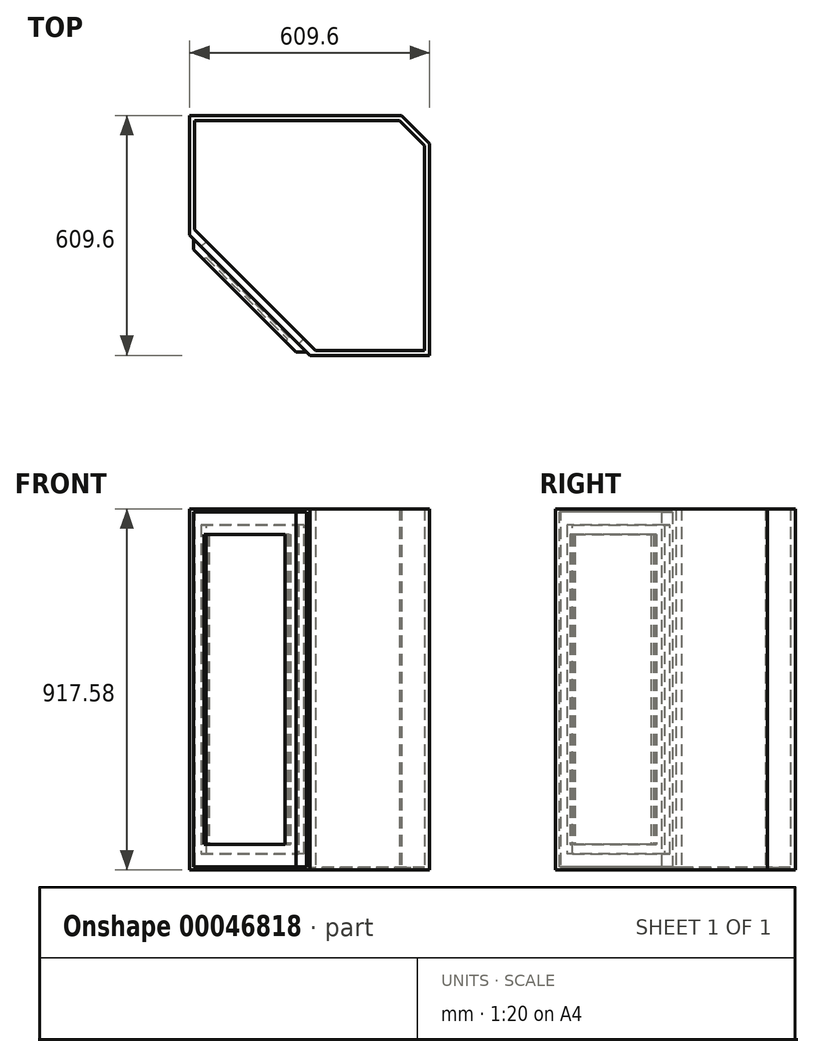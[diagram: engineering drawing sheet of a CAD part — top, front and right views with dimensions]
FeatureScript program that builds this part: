
annotation { "Feature Type Name" : "Feature", "Feature Type Description" : "" }
export const myFeature = defineFeature(function(context is Context, id is Id, definition is map)
    precondition{}
    {
        {
            var Q0;
            Q0=qCreatedBy(makeId("Top.planeOp"),FACE);
            var sketch = newSketch(context, id + "F0", { "sketchPlane" : qUnion([Q0])});
            skLineSegment(sketch, "E0.bottom", {"start": v(-304.8, 304.8) * mm, "end": v(304.8, 304.8) * mm, "construction": true});
            skLineSegment(sketch, "E0.top", {"start": v(-304.8, -304.8) * mm, "end": v(304.8, -304.8) * mm, "construction": true});
            skLineSegment(sketch, "E0.left", {"start": v(-304.8, 304.8) * mm, "end": v(-304.8, -304.8) * mm, "construction": true});
            skLineSegment(sketch, "E0.right", {"start": v(304.8, 304.8) * mm, "end": v(304.8, -304.8) * mm, "construction": true});
            skLineSegment(sketch, "E1", {"start": v(-304.8, 304.8) * mm, "end": v(304.8, -304.8) * mm, "construction": true});
            skLineSegment(sketch, "E2", {"start": v(-304.8, 0.53) * mm, "end": v(0.53, -304.8) * mm, "construction": true});
            skLineSegment(sketch, "E3", {"start": v(232.96, 304.8) * mm, "end": v(304.8, 232.96) * mm, "construction": true});
            skSolve(sketch);
        }
        {
            var Q0;
            Q0=qCreatedBy(makeId("Top.planeOp"),FACE);
            var sketch = newSketch(context, id + "F1", { "sketchPlane" : qUnion([Q0])});
            skLineSegment(sketch, "E4", {"start": v(-304.8, 0.53) * mm, "end": v(0.53, -304.8) * mm});
            skLineSegment(sketch, "E5", {"start": v(-304.8, 0.53) * mm, "end": v(-304.8, 27.47) * mm});
            skLineSegment(sketch, "E6", {"start": v(0.53, -304.8) * mm, "end": v(27.47, -304.8) * mm});
            skLineSegment(sketch, "E7", {"start": v(-304.8, 27.47) * mm, "end": v(27.47, -304.8) * mm});
            skLineSegment(sketch, "E8", {"start": v(-304.8, 27.47) * mm, "end": v(-304.8, 304.8) * mm});
            skLineSegment(sketch, "E9", {"start": v(27.47, -304.8) * mm, "end": v(304.8, -304.8) * mm});
            skLineSegment(sketch, "E10", {"start": v(304.8, -304.8) * mm, "end": v(304.8, 232.96) * mm});
            skLineSegment(sketch, "E11", {"start": v(-304.8, 304.8) * mm, "end": v(232.96, 304.8) * mm});
            skLineSegment(sketch, "E12", {"start": v(232.96, 304.8) * mm, "end": v(304.8, 232.96) * mm});
            skLineSegment(sketch, "E13", {"start": v(-292.1, 14.77) * mm, "end": v(-292.1, 292.1) * mm});
            skLineSegment(sketch, "E14", {"start": v(-292.1, 292.1) * mm, "end": v(227.7, 292.1) * mm});
            skLineSegment(sketch, "E15", {"start": v(227.7, 292.1) * mm, "end": v(292.1, 227.7) * mm});
            skLineSegment(sketch, "E16", {"start": v(292.1, 227.7) * mm, "end": v(292.1, -292.1) * mm});
            skLineSegment(sketch, "E17", {"start": v(292.1, -292.1) * mm, "end": v(14.77, -292.1) * mm});
            skSolve(sketch);
        }
        {
            var Q0;
            Q0=makeQuery(id+"F1.imprint","IMPRINT",FACE,{"disambiguationData":[TD([[makeQuery(id+"F1.imprint","IMPRINT",EDGE,{"derivedFrom":sQuery(id+"F1.wireOp",EDGE,"E4")}),1.0]])]});
            var Q1;
            {var subQ1=sQuery(id+"F1.wireOp",EDGE,"E8");Q1=makeQuery(id+"F1.imprint","IMPRINT",FACE,{"disambiguationData":[TD([[makeQuery(id+"F1.imprint","IMPRINT",EDGE,{"derivedFrom":subQ1}),-1.0]])]});}
            extrude(context, id + "F2", {"entities" : qUnion([Q0, Q1]), "depth" : 917.57 * mm});
        }
        {
            var Q0;
            {var subQ0=sQuery(id+"F1.wireOp",EDGE,"E4");Q0=makeQuery(id+"FLCiGweJVPZvpob_1.boolean.opBoolean","MERGE",FACE,{"derivedFrom":[makeQuery(id+"F2.opExtrude","SWEPT_FACE",FACE,{"disambiguationData":[OSD([subQ0])]}),makeQuery(id+"FLCiGweJVPZvpob_1.opExtrude","SWEPT_FACE",FACE,{"disambiguationData":[OSD([subQ0])]})]});}
            var sketch = newSketch(context, id + "F3", { "sketchPlane" : qUnion([Q0])});
            skLineSegment(sketch, "E18.bottom", {"start": v(-174.63, 876.3) * mm, "end": v(174.62, 876.3) * mm});
            skLineSegment(sketch, "E18.top", {"start": v(-174.62, 41.28) * mm, "end": v(174.63, 41.28) * mm});
            skLineSegment(sketch, "E18.left", {"start": v(-174.62, 876.3) * mm, "end": v(-174.62, 41.28) * mm});
            skLineSegment(sketch, "E18.right", {"start": v(174.62, 876.3) * mm, "end": v(174.63, 41.28) * mm});
            skSolve(sketch);
        }
        {
            var Q0;
            Q0 = qSketchRegion(id + "F3", true);
            var Q1;
            Q1=makeQuery(id+"F3.imprint","IMPRINT",FACE,{"disambiguationData":[TD([[makeQuery(id+"F3.imprint","IMPRINT",EDGE,{"derivedFrom":sQuery(id+"F3.wireOp",EDGE,"E18.bottom")}),-1.0]])]});
            extrude(context, id + "F4", {"entities" : qUnion([Q0, Q1]), "operationType" : NewBodyOperationType.REMOVE, "oppositeDirection" : true, "depth" : 25.4 * mm});
        }
        {
            var Q0;
            {var subQ0=sQuery(id+"F1.wireOp",EDGE,"E4");Q0=makeQuery(id+"FLCiGweJVPZvpob_1.boolean.opBoolean","MERGE",FACE,{"derivedFrom":[makeQuery(id+"F2.opExtrude","SWEPT_FACE",FACE,{"disambiguationData":[OSD([subQ0])]}),makeQuery(id+"FLCiGweJVPZvpob_1.opExtrude","SWEPT_FACE",FACE,{"disambiguationData":[OSD([subQ0])]})]});}
            var sketch = newSketch(context, id + "F5", { "sketchPlane" : qUnion([Q0])});
            skLineSegment(sketch, "E19.bottom", {"start": v(-203.2, 909.64) * mm, "end": v(203.2, 909.64) * mm});
            skLineSegment(sketch, "E19.top", {"start": v(-203.2, 7.94) * mm, "end": v(203.2, 7.94) * mm});
            skLineSegment(sketch, "E19.left", {"start": v(-203.2, 909.64) * mm, "end": v(-203.2, 7.94) * mm});
            skLineSegment(sketch, "E19.right", {"start": v(203.2, 909.64) * mm, "end": v(203.2, 7.94) * mm});
            skLineSegment(sketch, "E20.bottom", {"start": v(-146.05, 852.49) * mm, "end": v(146.05, 852.49) * mm});
            skLineSegment(sketch, "E20.top", {"start": v(-146.05, 65.09) * mm, "end": v(146.05, 65.09) * mm});
            skLineSegment(sketch, "E20.left", {"start": v(-146.05, 852.49) * mm, "end": v(-146.05, 65.09) * mm});
            skLineSegment(sketch, "E20.right", {"start": v(146.05, 852.49) * mm, "end": v(146.05, 65.09) * mm});
            skSolve(sketch);
        }
        {
            var Q0;
            Q0 = qSketchRegion(id + "F5", true);
            extrude(context, id + "F6", {"entities" : qUnion([Q0]), "depth" : 19.05 * mm});
        }
        {
            var Q0;
            Q0=makeQuery(id+"F6.opExtrude","SWEPT_FACE",FACE,{"disambiguationData":[OSD([sQuery(id+"F5.wireOp",EDGE,"E19.bottom")])]});
            var sketch = newSketch(context, id + "F7", { "sketchPlane" : qUnion([Q0])});
            skLineSegment(sketch, "E21", {"start": v(-8.45, -295.82) * mm, "end": v(-35.4, -295.82) * mm});
            skLineSegment(sketch, "E22", {"start": v(-8.45, -295.82) * mm, "end": v(-21.92, -309.3) * mm});
            skLineSegment(sketch, "E23", {"start": v(-21.92, -309.3) * mm, "end": v(-35.4, -295.82) * mm});
            skLineSegment(sketch, "E24", {"start": v(-295.82, -8.45) * mm, "end": v(-309.3, -21.92) * mm});
            skLineSegment(sketch, "E25", {"start": v(-309.3, -21.92) * mm, "end": v(-295.82, -35.4) * mm});
            skLineSegment(sketch, "E26", {"start": v(-295.82, -35.4) * mm, "end": v(-295.82, -8.45) * mm});
            skSolve(sketch);
        }
        {
            var Q0;
            Q0 = qSketchRegion(id + "F7", true);
            extrude(context, id + "F8", {"entities" : qUnion([Q0]), "operationType" : NewBodyOperationType.REMOVE, "endBound" : BoundingType.THROUGH_ALL, "oppositeDirection" : true, "depth" : 25.4 * mm});
        }
        {
            var Q0;
            Q0=makeQuery(id+"F6.opExtrude","SWEPT_FACE",FACE,{"disambiguationData":[OSD([sQuery(id+"F5.wireOp",EDGE,"E20.top")])]});
            var sketch = newSketch(context, id + "F9", { "sketchPlane" : qUnion([Q0])});
            skLineSegment(sketch, "E27", {"start": v(-258.78, -52.23) * mm, "end": v(-263.27, -56.72) * mm});
            skLineSegment(sketch, "E28", {"start": v(-52.23, -258.78) * mm, "end": v(-56.72, -263.27) * mm});
            skLineSegment(sketch, "E29", {"start": v(-52.23, -258.78) * mm, "end": v(-258.78, -52.23) * mm});
            skLineSegment(sketch, "E30", {"start": v(-263.27, -56.72) * mm, "end": v(-56.72, -263.27) * mm});
            skSolve(sketch);
        }
        {
            var Q0;
            Q0 = qSketchRegion(id + "F9", true);
            extrude(context, id + "F10", {"entities" : qUnion([Q0]), "operationType" : NewBodyOperationType.ADD, "endBound" : BoundingType.UP_TO_NEXT, "depth" : 25.4 * mm});
        }
        {
            var Q0;
            {var subQ0=sQuery(id+"F1.wireOp",EDGE,"E13");Q0=makeQuery(id+"F1.imprint","IMPRINT",FACE,{"disambiguationData":[TD([[makeQuery(id+"F1.imprint","IMPRINT",EDGE,{"derivedFrom":subQ0}),-1.0]])]});}
            extrude(context, id + "F11", {"entities" : qUnion([Q0]), "operationType" : NewBodyOperationType.ADD, "depth" : 6.35 * mm});
        }
    });
